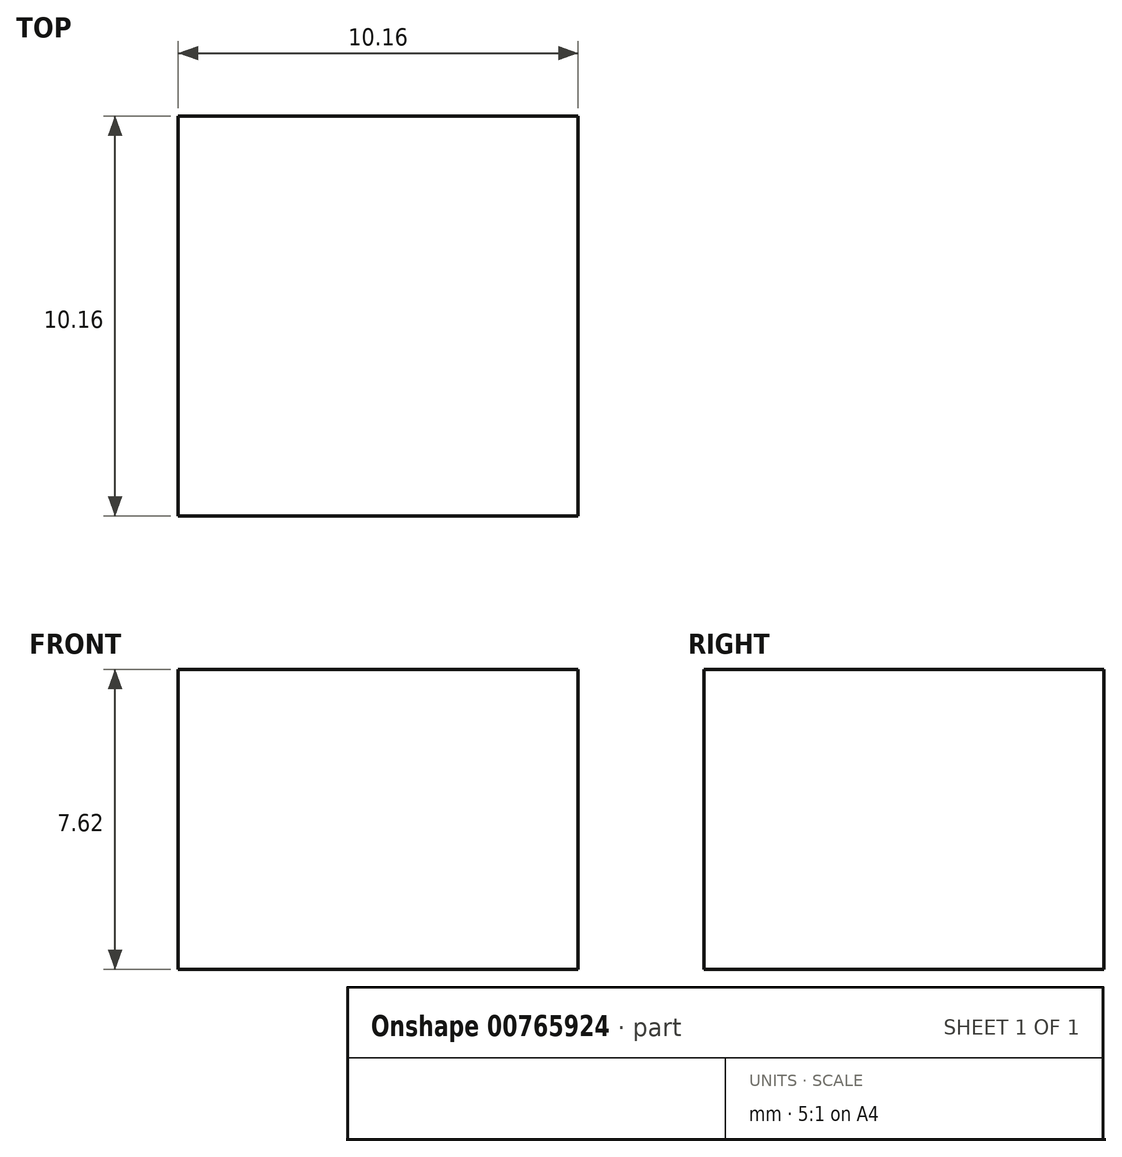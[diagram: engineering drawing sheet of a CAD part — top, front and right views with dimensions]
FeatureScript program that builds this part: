
annotation { "Feature Type Name" : "Feature", "Feature Type Description" : "" }
export const myFeature = defineFeature(function(context is Context, id is Id, definition is map)
    precondition{}
    {
        {
            var Q0;
            Q0=qCreatedBy(makeId("Top.planeOp"),FACE);
            var sketch = newSketch(context, id + "F0", { "sketchPlane" : qUnion([Q0])});
            skLineSegment(sketch, "E0.bottom", {"start": v(0, 0) * mm, "end": v(10.16, 0) * mm});
            skLineSegment(sketch, "E0.top", {"start": v(0, -10.16) * mm, "end": v(10.16, -10.16) * mm});
            skLineSegment(sketch, "E0.left", {"start": v(0, 0) * mm, "end": v(0, -10.16) * mm});
            skLineSegment(sketch, "E0.right", {"start": v(10.16, 0) * mm, "end": v(10.16, -10.16) * mm});
            skSolve(sketch);
        }
        {
            var Q0;
            Q0=makeQuery(id+"F0.imprint","IMPRINT",FACE,{"disambiguationData":[TD([[makeQuery(id+"F0.imprint","IMPRINT",EDGE,{"derivedFrom":sQuery(id+"F0.wireOp",EDGE,"E0.bottom")}),-1.0]])]});
            extrude(context, id + "F1", {"entities" : qUnion([Q0]), "depth" : 7.62 * mm, "offsetDistance" : 25.4 * mm});
        }
    });
